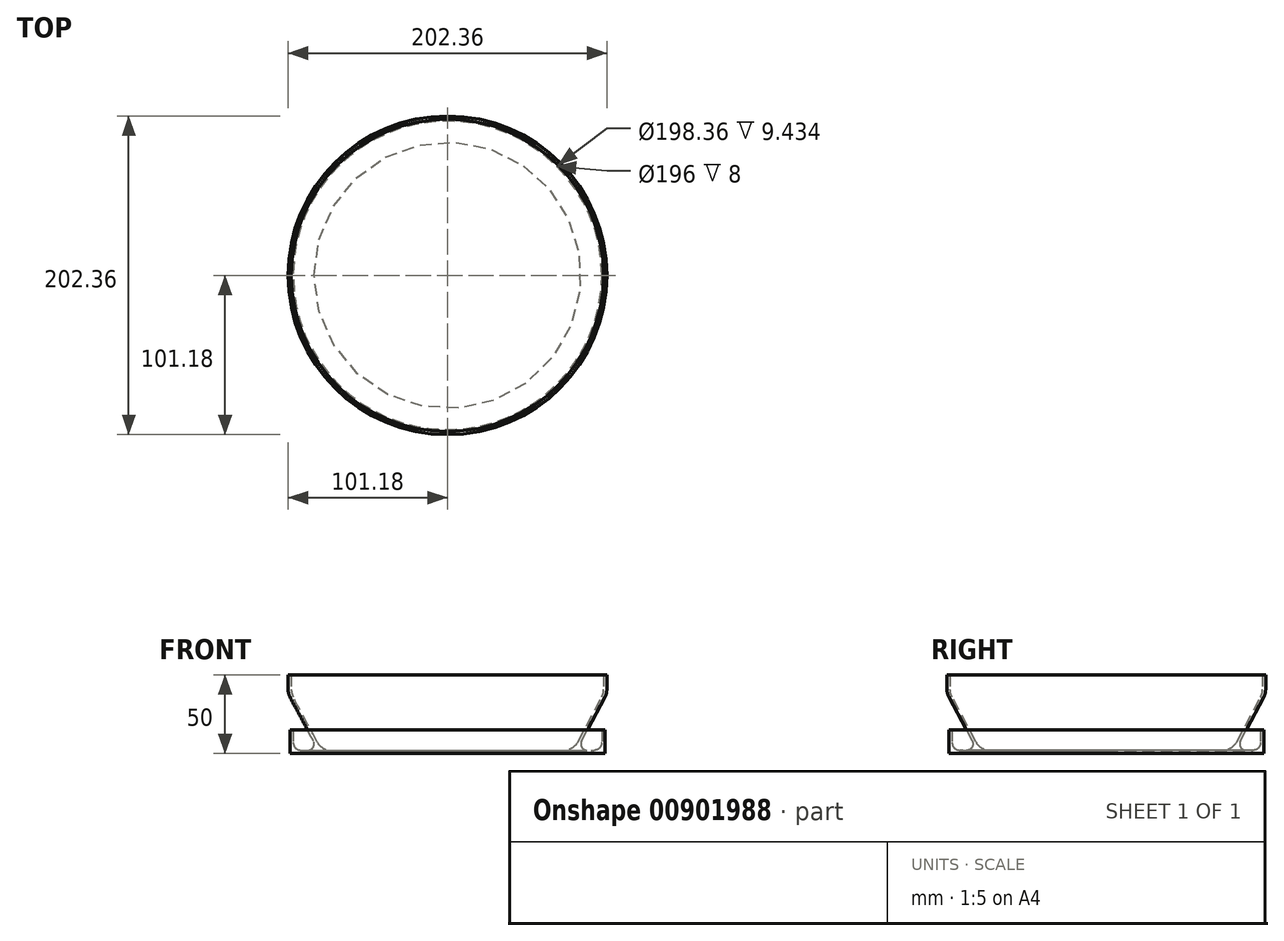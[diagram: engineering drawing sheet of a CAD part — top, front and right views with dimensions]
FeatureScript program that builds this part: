
annotation { "Feature Type Name" : "Feature", "Feature Type Description" : "" }
export const myFeature = defineFeature(function(context is Context, id is Id, definition is map)
    precondition{}
    {
        {
            var Q0;
            Q0=qCreatedBy(makeId("Front.planeOp"),FACE);
            var sketch = newSketch(context, id + "F0", { "sketchPlane" : qUnion([Q0])});
            skLineSegment(sketch, "E0", {"start": v(0, 0) * mm, "end": v(-74, 0) * mm});
            skLineSegment(sketch, "E1", {"start": v(-82.82, 5.3) * mm, "end": v(-99.18, 36.07) * mm});
            skLineSegment(sketch, "E2.0", {"start": v(-85.16, 5.88) * mm, "end": v(-101.18, 36) * mm});
            skLineSegment(sketch, "E3.0", {"start": v(0, -2) * mm, "end": v(-100, -2) * mm});
            skLineSegment(sketch, "E4", {"start": v(0, -2) * mm, "end": v(0, 0) * mm});
            skLineSegment(sketch, "E5", {"start": v(-100, -2) * mm, "end": v(-100, 13) * mm});
            skLineSegment(sketch, "E6", {"start": v(-100, 13) * mm, "end": v(-98, 13) * mm});
            skLineSegment(sketch, "E7", {"start": v(-98, 13) * mm, "end": v(-98, 5) * mm});
            skLineSegment(sketch, "E8", {"start": v(-93, 0) * mm, "end": v(-88.7, 0) * mm});
            skPoint(sketch, "E9.visualSharp", {"position": v(-98, 0) * mm});
            skArc(sketch, "E9.filletArc", {"start": v(-98, 5) * mm, "mid": v(-96.54, 1.46) * mm, "end": v(-93, 0) * mm});
            skPoint(sketch, "E10.visualSharp", {"position": v(-80, 0) * mm});
            skArc(sketch, "E10.filletArc", {"start": v(-82.82, 5.3) * mm, "mid": v(-79.14, 1.43) * mm, "end": v(-74, 0) * mm});
            skPoint(sketch, "E11.visualSharp", {"position": v(-82.04, 0) * mm});
            skArc(sketch, "E11.filletArc", {"start": v(-88.7, 0) * mm, "mid": v(-85.27, 1.94) * mm, "end": v(-85.16, 5.88) * mm});
            skLineSegment(sketch, "E12", {"start": v(-101.18, 36) * mm, "end": v(-101.18, 48) * mm});
            skLineSegment(sketch, "E13", {"start": v(-101.18, 48) * mm, "end": v(-99.18, 48) * mm});
            skLineSegment(sketch, "E14", {"start": v(-99.18, 48) * mm, "end": v(-99.18, 36.07) * mm});
            skPoint(sketch, "E15.orphan", {"position": v(-98.78, 35.32) * mm});
            skSolve(sketch);
        }
        {
            var Q0;
            Q0=makeQuery(id+"F0.imprint","IMPRINT",FACE,{"disambiguationData":[TD([[makeQuery(id+"F0.imprint","IMPRINT",EDGE,{"derivedFrom":sQuery(id+"F0.wireOp",EDGE,"E0")}),1.0]])]});
            var Q1;
            Q1=sQuery(id+"F0.wireOp",EDGE,"E4");
            revolve(context, id + "F1", {"surfaceOperationType" : NewSurfaceOperationType.NEW, "entities" : qUnion([Q0]), "axis" : qUnion([Q1]), "revolveType" : RevolveType.FULL});
        }
        {
            var Q0;
            Q0=makeQuery(id+"F1.opRevolve","SWEPT_EDGE",EDGE,{"disambiguationData":[OSD([sQuery(id+"F0.wireOp",EDGE,"E1"),sQuery(id+"F0.wireOp",EDGE,"E14")])]});
            var Q1;
            Q1=makeQuery(id+"F1.opRevolve","SWEPT_EDGE",EDGE,{"disambiguationData":[OSD([sQuery(id+"F0.wireOp",EDGE,"E2.0"),sQuery(id+"F0.wireOp",EDGE,"E12")])]});
            fillet(context, id + "F2", {"entities" : qUnion([Q0, Q1]), "radius" : 10 * mm, "tangentPropagation" : true, "allowEdgeOverflow" : false});
        }
    });
